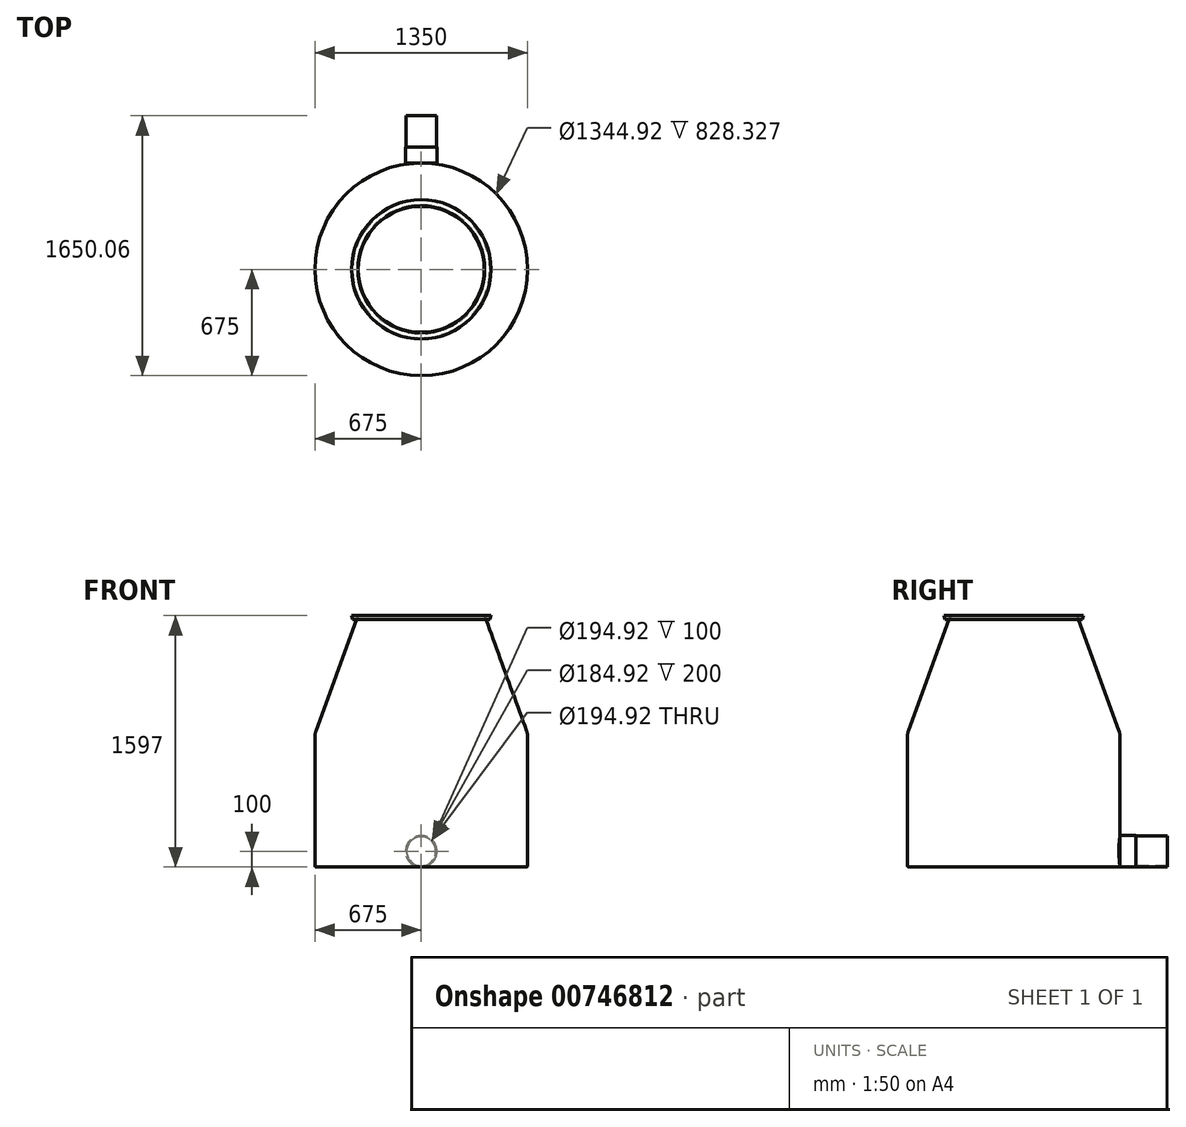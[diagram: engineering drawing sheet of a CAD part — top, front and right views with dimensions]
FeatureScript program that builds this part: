
annotation { "Feature Type Name" : "Feature", "Feature Type Description" : "" }
export const myFeature = defineFeature(function(context is Context, id is Id, definition is map)
    precondition{}
    {
        {
            var Q0;
            Q0=qCreatedBy(makeId("Top.planeOp"),FACE);
            var sketch = newSketch(context, id + "F0", { "sketchPlane" : qUnion([Q0])});
            skCircle(sketch, "E0", {"center": v(0, 0) * mm, "radius": 675 * mm});
            skSolve(sketch);
        }
        {
            var Q0;
            Q0=qSketchRegion(id+"F0",true);
            extrude(context, id + "F1", {"entities" : qUnion([Q0]), "depth" : 848.5 * mm, "offsetDistance" : 25.4 * mm});
        }
        {
            var Q0;
            Q0=makeQuery(id+"F1.opExtrude","CAP_FACE",FACE,{"disambiguationData":[OSD([sQuery(id+"F0.wireOp",EDGE,"E0")])],"isStart":false});
            var sketch = newSketch(context, id + "F2", { "sketchPlane" : qUnion([Q0])});
            skCircle(sketch, "E1", {"center": v(0, 0) * mm, "radius": 675 * mm});
            skSolve(sketch);
        }
        {
            var Q0;
            Q0=qSketchRegion(id+"F2",true);
            extrude(context, id + "F3", {"entities" : qUnion([Q0]), "operationType" : NewBodyOperationType.ADD, "depth" : 848.5 * mm - 100 * mm, "offsetDistance" : 25.4 * mm, "hasDraft" : true, "draftAngle" : 20 * degree, "draftPullDirection" : true});
        }
        {
            var Q0;
            Q0=makeQuery(id+"F3.boolean.opBoolean","MERGE",EDGE,{"derivedFrom":[makeQuery(id+"F1.opExtrude","CAP_EDGE",EDGE,{"disambiguationData":[OSD([sQuery(id+"F0.wireOp",EDGE,"E0")])],"isStart":false}),makeQuery(id+"F3.opExtrude","CAP_EDGE",EDGE,{"disambiguationData":[OSD([sQuery(id+"F2.wireOp",EDGE,"E1")])],"isStart":true})]});
            fillet(context, id + "F4", {"entities" : qUnion([Q0]), "radius" : 100 * mm, "tangentPropagation" : true, "allowEdgeOverflow" : false});
        }
        {
            var Q0;
            Q0=makeQuery(id+"F3.opExtrude","CAP_FACE",FACE,{"disambiguationData":[OSD([sQuery(id+"F2.wireOp",EDGE,"E1")])],"isStart":false});
            shell(context, id + "F5", {"entities" : qUnion([Q0]), "thickness" : 2.54 * mm});
        }
        {
            var Q0;
            Q0=makeQuery(id+"F3.opExtrude","CAP_FACE",FACE,{"disambiguationData":[OSD([sQuery(id+"F2.wireOp",EDGE,"E1")])],"isStart":false});
            var sketch = newSketch(context, id + "F6", { "sketchPlane" : qUnion([Q0])});
            skCircle(sketch, "E2", {"center": v(0, 0) * mm, "radius": 442.57 * mm});
            skSolve(sketch);
        }
        {
            var Q0;
            Q0=makeQuery(id+"F6.imprint","IMPRINT",FACE,{"disambiguationData":[TD([[makeQuery(id+"F6.imprint","IMPRINT",EDGE,{"derivedFrom":sQuery(id+"F6.wireOp",EDGE,"E2")}),1.0]])]});
            extrude(context, id + "F7", {"entities" : qUnion([Q0]), "oppositeDirection" : true, "depth" : 25.4 * mm, "offsetDistance" : 25.4 * mm, "hasDraft" : true, "draftAngle" : 15 * degree, "draftPullDirection" : true});
        }
        {
            var Q0;
            Q0=makeQuery(id+"F1.opExtrude","CAP_EDGE",EDGE,{"disambiguationData":[OSD([sQuery(id+"F0.wireOp",EDGE,"E0")])],"isStart":true});
            fillet(context, id + "F8", {"entities" : qUnion([Q0]), "radius" : 8 * mm, "tangentPropagation" : true, "allowEdgeOverflow" : false});
        }
        {
            var Q0;
            Q0=makeQuery(id+"F3.opExtrude","SWEPT_FACE",FACE,{"disambiguationData":[OSD([sQuery(id+"F2.wireOp",EDGE,"E1")])]});
            fillet(context, id + "F9", {"entities" : qUnion([Q0]), "radius" : 8 * mm, "tangentPropagation" : true, "allowEdgeOverflow" : false});
        }
        {
            var Q0;
            Q0=qCreatedBy(makeId("Front.planeOp"),FACE);
            cPlane(context, id + "F10", {"entities" : qUnion([Q0]), "cplaneType" : CPlaneType.OFFSET, "offset" : 675.06 * mm, "oppositeDirection" : true, "width" : 152.4 * mm, "height" : 152.4 * mm});
        }
        {
            var Q0;
            Q0=qCreatedBy(id+"F10.planeOp",FACE);
            var sketch = newSketch(context, id + "F11", { "sketchPlane" : qUnion([Q0])});
            skCircle(sketch, "E3", {"center": v(0, 100) * mm, "radius": 100 * mm});
            skSolve(sketch);
        }
        {
            var Q0;
            Q0=qSketchRegion(id+"F11",true);
            extrude(context, id + "F12", {"entities" : qUnion([Q0]), "oppositeDirection" : true, "depth" : 100 * mm, "offsetDistance" : 25.4 * mm});
        }
        {
            var Q0;
            Q0=makeQuery(id+"F12.opExtrude","CAP_FACE",FACE,{"disambiguationData":[OSD([sQuery(id+"F11.wireOp",EDGE,"E3")])],"isStart":false});
            shell(context, id + "F13", {"entities" : qUnion([Q0]), "thickness" : 2.54 * mm});
        }
        {
            var Q0;
            {var subQ0=sQuery(id+"F11.wireOp",EDGE,"E3");Q0=makeQuery(id+"F13.opShell","OFFSET_FACE",FACE,{"disambiguationData":[OSD([subQ0]),TDD([makeQuery(id+"F12.opExtrude","CAP_FACE",FACE,{"disambiguationData":[OSD([subQ0])],"isStart":true})])]});}
            extrude(context, id + "F14", {"entities" : qUnion([Q0]), "operationType" : NewBodyOperationType.REMOVE, "oppositeDirection" : true, "depth" : 416.56 * mm, "offsetDistance" : 25.4 * mm});
        }
        {
            var Q0;
            Q0=qCreatedBy(id+"F10.planeOp",FACE);
            var sketch = newSketch(context, id + "F15", { "sketchPlane" : qUnion([Q0])});
            skCircle(sketch, "E4", {"center": v(0, 100) * mm, "radius": 97.46 * mm});
            skSolve(sketch);
        }
        {
            var Q0;
            Q0=qSketchRegion(id+"F15",true);
            extrude(context, id + "F16", {"entities" : qUnion([Q0]), "operationType" : NewBodyOperationType.REMOVE, "depth" : 80.52 * mm, "offsetDistance" : 25.4 * mm});
        }
        {
            var Q0;
            Q0=makeQuery(id+"F12.opExtrude","CAP_FACE",FACE,{"disambiguationData":[OSD([sQuery(id+"F11.wireOp",EDGE,"E3")])],"isStart":false});
            var sketch = newSketch(context, id + "F17", { "sketchPlane" : qUnion([Q0])});
            skCircle(sketch, "E5", {"center": v(0, 100) * mm, "radius": 97.46 * mm});
            skSolve(sketch);
        }
        {
            var Q0;
            Q0=qSketchRegion(id+"F17",true);
            extrude(context, id + "F18", {"entities" : qUnion([Q0]), "depth" : 200 * mm, "offsetDistance" : 25.4 * mm});
        }
        {
            var Q0;
            Q0=makeQuery(id+"F18.opExtrude","CAP_FACE",FACE,{"disambiguationData":[OSD([sQuery(id+"F17.wireOp",EDGE,"E5")])],"isStart":true});
            var sketch = newSketch(context, id + "F19", { "sketchPlane" : qUnion([Q0])});
            skCircle(sketch, "E6", {"center": v(0, 100) * mm, "radius": 92.46 * mm});
            skSolve(sketch);
        }
        {
            var Q0;
            Q0=qSketchRegion(id+"F19",true);
            extrude(context, id + "F20", {"entities" : qUnion([Q0]), "operationType" : NewBodyOperationType.REMOVE, "oppositeDirection" : true, "depth" : 226.06 * mm, "offsetDistance" : 25.4 * mm});
        }
    });
